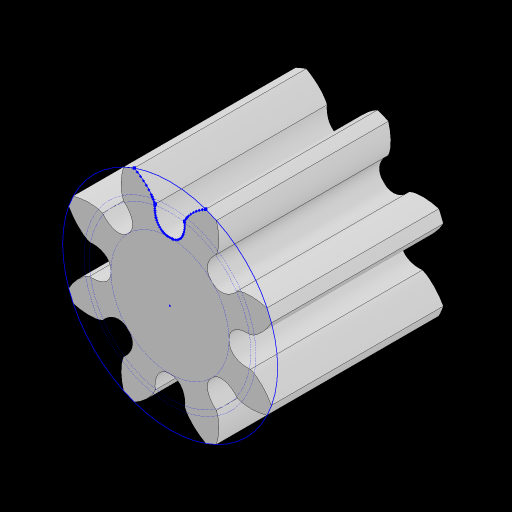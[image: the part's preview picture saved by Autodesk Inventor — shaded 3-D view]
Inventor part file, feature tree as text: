
AUTODESK INVENTOR PART (.ipt)
format: ipt  version: 2023.2 (Build 272271030, 271C)  size: 196,096 bytes
history: native  units: mm
features: extrude x2, sketch x1, pattern_circular x1
ambient origin geometry x8: Origin, YZ Plane, XZ Plane, XY Plane, X Axis, Y Axis, Z Axis, Center Point
bodies: Solid1 (feature_tree)
feature tree (4):
  sketch  "Sketch1"  dims[d0=10.0mm d1=0.0mm d2=0.0mm d3=0.0mm d4=80.0mm d5=360.0deg]
  extrude  "Extrusion1"  TaperAngle=0.0deg  [1 undecoded]
  extrude  "Extrusion2"  Depth=80.0mm TaperAngle=360.0deg
  pattern_circular  "Circular Pattern1"  [2 undecoded]
note: 3 required parameter values undecoded (feature->parameter linkage not recoverable at this tier; creation-order binding heuristic only, values carry confidence <= 0.55)
